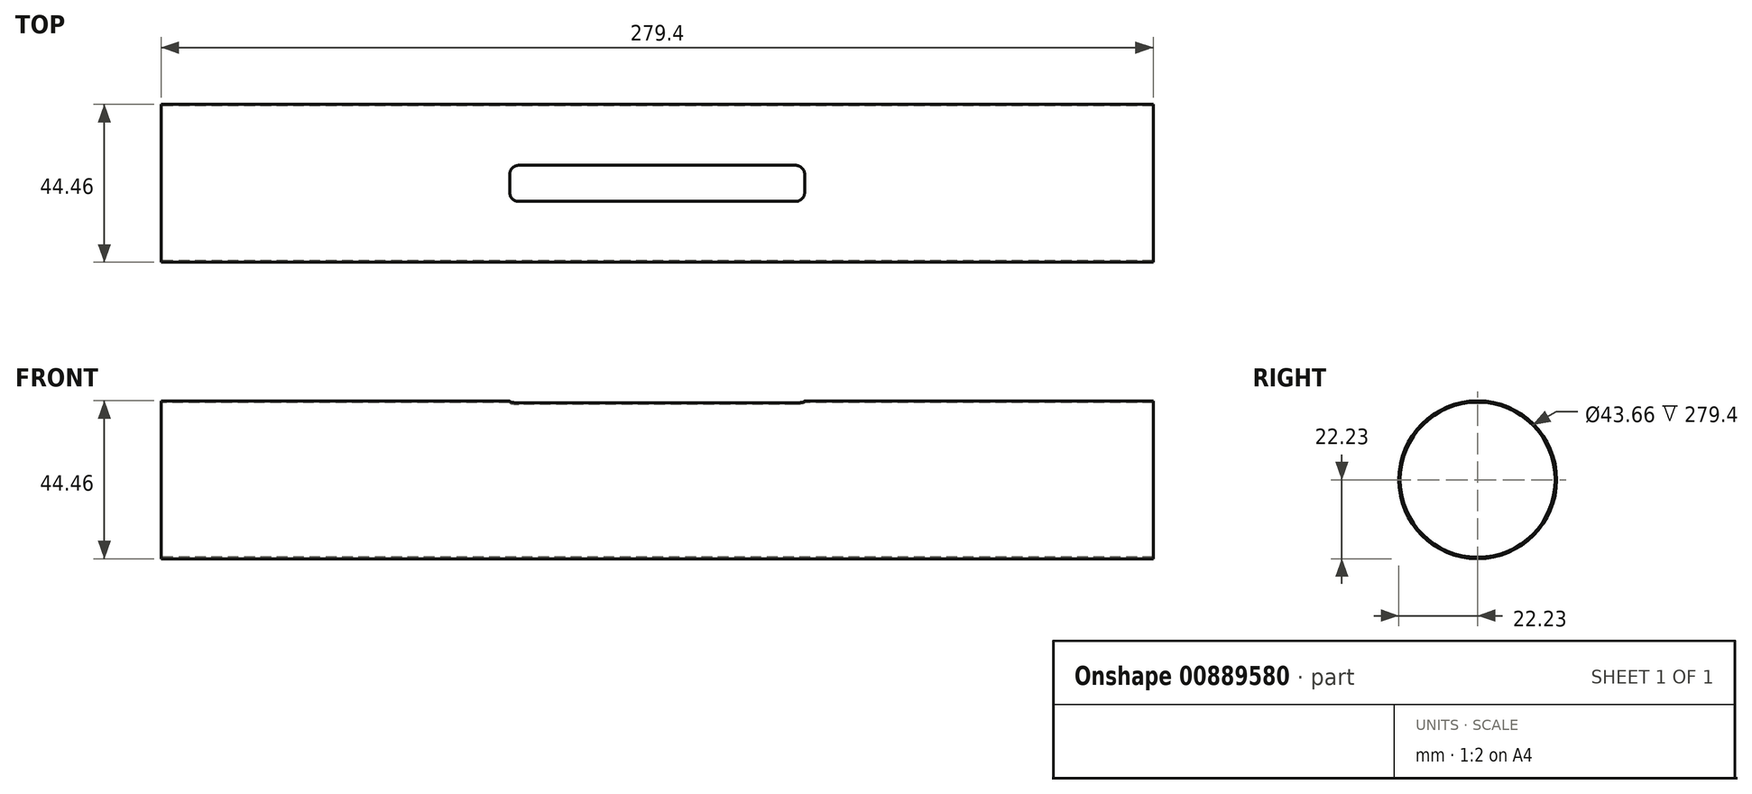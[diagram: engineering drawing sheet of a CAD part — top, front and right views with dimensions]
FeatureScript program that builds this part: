
annotation { "Feature Type Name" : "Feature", "Feature Type Description" : "" }
export const myFeature = defineFeature(function(context is Context, id is Id, definition is map)
    precondition{}
    {
        {
            var Q0;
            Q0=qCreatedBy(makeId("Right.planeOp"),FACE);
            var sketch = newSketch(context, id + "F0", { "sketchPlane" : qUnion([Q0])});
            skCircle(sketch, "E0", {"center": v(0, 0) * mm, "radius": 22.23 * mm});
            skCircle(sketch, "E1", {"center": v(0, 0) * mm, "radius": 21.83 * mm});
            skSolve(sketch);
        }
        {
            var Q0;
            Q0=makeQuery(id+"F0.imprint","IMPRINT",FACE,{"disambiguationData":[TD([[makeQuery(id+"F0.imprint","IMPRINT",EDGE,{"derivedFrom":sQuery(id+"F0.wireOp",EDGE,"E0")}),1.0]])]});
            extrude(context, id + "F1", {"entities" : qUnion([Q0]), "endBound" : BoundingType.SYMMETRIC, "depth" : 279.4 * mm, "offsetDistance" : 25.4 * mm});
        }
        {
            var Q0;
            Q0=qCreatedBy(makeId("Top.planeOp"),FACE);
            var sketch = newSketch(context, id + "F2", { "sketchPlane" : qUnion([Q0])});
            skLineSegment(sketch, "E2.bottom", {"start": v(-38.99, 5.08) * mm, "end": v(38.99, 5.08) * mm});
            skLineSegment(sketch, "E2.top", {"start": v(-38.99, -5.08) * mm, "end": v(38.99, -5.08) * mm});
            skLineSegment(sketch, "E2.left", {"start": v(-41.53, 2.54) * mm, "end": v(-41.53, -2.54) * mm});
            skLineSegment(sketch, "E2.right", {"start": v(41.53, 2.54) * mm, "end": v(41.53, -2.54) * mm});
            skPoint(sketch, "E2.middle", {"position": v(0, 0) * mm});
            skPoint(sketch, "E3.visualSharp", {"position": v(-41.53, 5.08) * mm});
            skArc(sketch, "E3.filletArc", {"start": v(-38.99, 5.08) * mm, "mid": v(-40.79, 4.34) * mm, "end": v(-41.53, 2.54) * mm});
            skPoint(sketch, "E4.visualSharp", {"position": v(-41.53, -5.08) * mm});
            skArc(sketch, "E4.filletArc", {"start": v(-41.53, -2.54) * mm, "mid": v(-40.79, -4.34) * mm, "end": v(-38.99, -5.08) * mm});
            skPoint(sketch, "E5.visualSharp", {"position": v(41.53, 5.08) * mm});
            skArc(sketch, "E5.filletArc", {"start": v(41.53, 2.54) * mm, "mid": v(40.79, 4.34) * mm, "end": v(38.99, 5.08) * mm});
            skPoint(sketch, "E6.visualSharp", {"position": v(41.53, -5.08) * mm});
            skArc(sketch, "E6.filletArc", {"start": v(38.99, -5.08) * mm, "mid": v(40.79, -4.34) * mm, "end": v(41.53, -2.54) * mm});
            skSolve(sketch);
        }
        {
            var Q0;
            Q0 = qSketchRegion(id + "F2", true);
            extrude(context, id + "F3", {"entities" : qUnion([Q0]), "operationType" : NewBodyOperationType.REMOVE, "depth" : 25.4 * mm, "offsetDistance" : 25.4 * mm});
        }
    });
